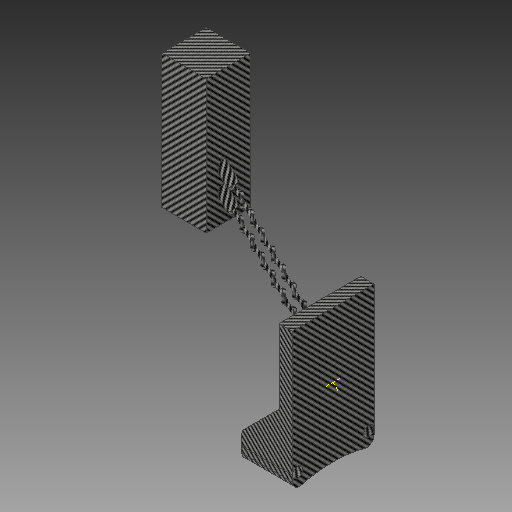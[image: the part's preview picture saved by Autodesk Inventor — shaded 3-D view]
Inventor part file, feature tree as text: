
AUTODESK INVENTOR PART (.ipt)
format: ipt  version: 2018 (Build 220112000, 112)  size: 652,800 bytes
history: native  units: mm
features: sketch x25, extrude x23, other x16, plane x5, fillet x3, helix x2, mirror x1
ambient origin geometry x8: Origin, YZ Plane, XZ Plane, XY Plane, X Axis, Y Axis, Z Axis, Center Point
bodies: Solid1 (feature_tree)
feature tree (75):
  extrude  "Extrusion1"  Depth=34.0mm
  extrude  "Extrusion2"  Depth=34.0mm
  extrude  "Extrusion3"  Depth=9.0mm TaperAngle=0.0deg
  extrude  "Extrusion4"  Depth=7.0mm
  extrude  "Extrusion5"  Depth=50.0mm
  extrude  "Extrusion7"  Depth=9.0mm
  extrude  "Extrusion9"  Depth=7.0mm
  plane  "Work Plane4"
  extrude  "Extrusion11"  Depth=5.0mm TaperAngle=0.0deg
  other  "UCS1"
  other  "UCS2"
  sketch  "Sketch18"  dims[d12=45.0deg d13=9.0mm]
  extrude  "Extrusion12"  Depth=20.0mm TaperAngle=0.0deg
  extrude  "Extrusion13"  Depth=14.414mm
  helix  "Coil1"  [1 undecoded]
  extrude  "Extrusion14"  Depth=10.0mm
  sketch  "Sketch25"  dims[d51=10.0mm d52=7.0mm]
  extrude  "Extrusion15"  Depth=200.0mm TaperAngle=0.0deg
  sketch  "Sketch27"  dims[d56=0.0mm d57=0.0mm d58=0.0mm d59=0.0mm d60=0.0mm d61=0.0mm]
  sketch  "Sketch28"  dims[d62=0.0mm d63=0.0mm d64=0.0mm d65=0.0mm d66=0.0mm d67=0.0mm d68=5.0mm]
  helix  "Coil2"  [1 undecoded]
  plane  "Work Plane5"
  extrude  "Extrusion16"  Depth=18.0mm TaperAngle=0.0deg
  plane  "Work Plane6"
  extrude  "Extrusion17"  Depth=5.0mm
  plane  "Work Plane7"
  extrude  "Extrusion18"  Depth=18.0mm TaperAngle=0.0deg
  extrude  "Extrusion19"  Depth=10.0mm
  mirror  "Mirror1"
  extrude  "Extrusion20"  Depth=80.0mm
  extrude  "Extrusion21"  Depth=5.0mm TaperAngle=0.0deg
  extrude  "Extrusion22"  Depth=5.0mm
  extrude  "Extrusion23"  Depth=90.0mm
  fillet  "Fillet1"  Radius=15.0mm
  fillet  "Fillet2"  Radius=15.0mm
  extrude  "Extrusion24"  Depth=10.0mm TaperAngle=0.0deg
  plane  "Work Plane10"
  extrude  "Extrusion27"  Depth=10.0mm TaperAngle=0.0deg
  fillet  "Fillet4"  Radius=10.0mm
  extrude  "Extrusion28"  Depth=2.0mm TaperAngle=0.0deg
  sketch  "Sketch1"  dims[d0=34.0mm d1=55.0mm]
  sketch  "Sketch2"  dims[d2=90.0deg d3=34.0mm]
  sketch  "Sketch5"  dims[d4=90.0deg d5=9.0mm d6=0.0mm]
  sketch  "Sketch15"  dims[d7=7.0mm d8=7.0mm]
  sketch  "Sketch17"  dims[d9=1000.0mm d10=0.0mm d11=50.0mm]
  sketch  "Sketch19"  dims[d14=55.0mm d15=0.0mm d16=7.0mm]
  sketch  "Sketch21"  dims[d17=30.0mm d18=0.0mm d19=5.0mm d20=0.0mm]
  sketch  "Sketch23"  dims[d25=9.0mm d26=0.0mm d39=20.0mm d40=0.0mm]
  sketch  "Sketch24"  dims[d48=45.0deg d49=14.414mm d50=7.0mm]
  sketch  "Sketch26"  dims[d53=7.0mm d54=200.0mm d55=0.0mm]
  sketch  "Sketch29"  dims[d69=20.0mm d70=0.0mm d74=18.0mm d75=0.0mm]
  sketch  "Sketch30"  dims[d83=10.0mm d84=80.0mm d85=80.0mm d86=0.0mm d87=90.0deg d88=90.0deg d89=0.0mm d90=0.0mm d91=5.0mm]
  sketch  "Sketch31"  dims[d92=20.0mm d93=0.0mm d94=18.0mm d95=0.0mm]
  sketch  "Sketch32"  dims[d96=2.0mm]
  sketch  "Sketch33"  dims[d103=10.0mm d104=80.0mm d105=80.0mm d106=0.0mm d107=90.0deg d108=90.0deg d109=0.0mm d110=0.0mm d111=80.0mm]
  sketch  "Sketch34"  dims[d112=50.0mm d113=0.0mm d114=80.0mm]
  sketch  "Sketch36"  dims[d115=50.0mm d116=0.0mm d117=5.0mm d118=0.0mm]
  sketch  "Sketch37"  dims[d119=5.0mm d120=0.0mm d121=80.0mm]
  sketch  "Sketch39"  dims[d122=30.0mm d123=90.0mm d124=15.0mm d125=0.0mm d126=15.0mm d127=0.0mm]
  sketch  "Sketch44"  dims[d128=9.0mm d129=0.0mm d130=10.0mm d131=0.0mm]
  sketch  "Sketch45"  dims[d132=10.0mm d133=0.0mm d134=10.0mm d135=0.0mm d136=10.0mm d137=0.0mm d138=900.0mm d139=0.0mm d140=900.0mm d141=0.0mm d142=2.0mm d143=90.0mm d144=0.0mm d145=2.0mm d146=90.0mm d147=0.0mm d148=5.0mm d149=5.0mm d150=90.0mm d151=0.0mm d152=10.0mm d153=0.0mm d163=10.0mm d164=5.0mm d165=0.0mm d166=2.5mm d167=0.0mm d168=3.0mm d169=26.0mm d170=26.0mm d171=2.0mm d172=0.0mm]
  other  "UCS1: YZ Plane"
  other  "UCS1: XZ Plane"
  other  "UCS1: XY Plane"
  other  "UCS1: X Axis"
  other  "UCS1: Y Axis"
  other  "UCS1: Z Axis"
  other  "UCS1: Center Point"
  other  "UCS2: YZ Plane"
  other  "UCS2: XZ Plane"
  other  "UCS2: XY Plane"
  other  "UCS2: X Axis"
  other  "UCS2: Y Axis"
  other  "UCS2: Z Axis"
  other  "UCS2: Center Point"
note: 2 required parameter values undecoded (feature->parameter linkage not recoverable at this tier; creation-order binding heuristic only, values carry confidence <= 0.55)
